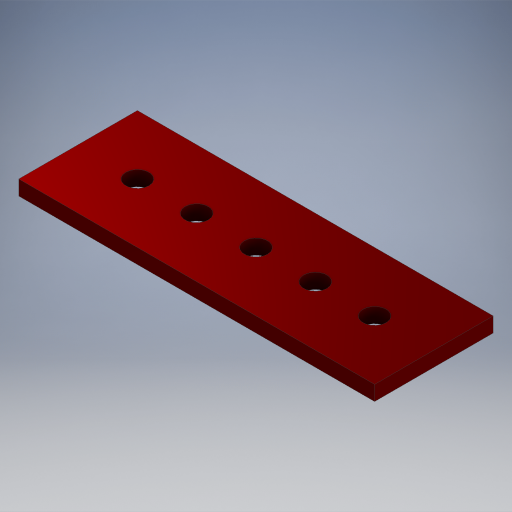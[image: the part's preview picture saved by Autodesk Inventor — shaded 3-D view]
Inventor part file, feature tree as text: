
AUTODESK INVENTOR PART (.ipt)
format: ipt  version: 2024.2 (Build 282272000, 272)  size: 266,752 bytes
history: native  units: in
note: dims shown in document units (in); Inventor stores cm internally (conversion verified against a paired STEP export)
features: extrude x1, sketch x1
ambient origin geometry x8: Origin, YZ Plane, XZ Plane, XY Plane, X Axis, Y Axis, Z Axis, Center Point
bodies: Solid1 (feature_tree)
feature tree (2):
  extrude  "Extrusion1"  Depth=1.0in
  sketch  "Sketch1"  dims[d0=3.0in d1=1.0in d2=0.196in d3=0.5in d4=0.5in d5=1.9685in d7=0.5in d8=0.3937in d10=1.0in d12=0.5in d13=0.5in d14=0.125in d15=0.0in]
